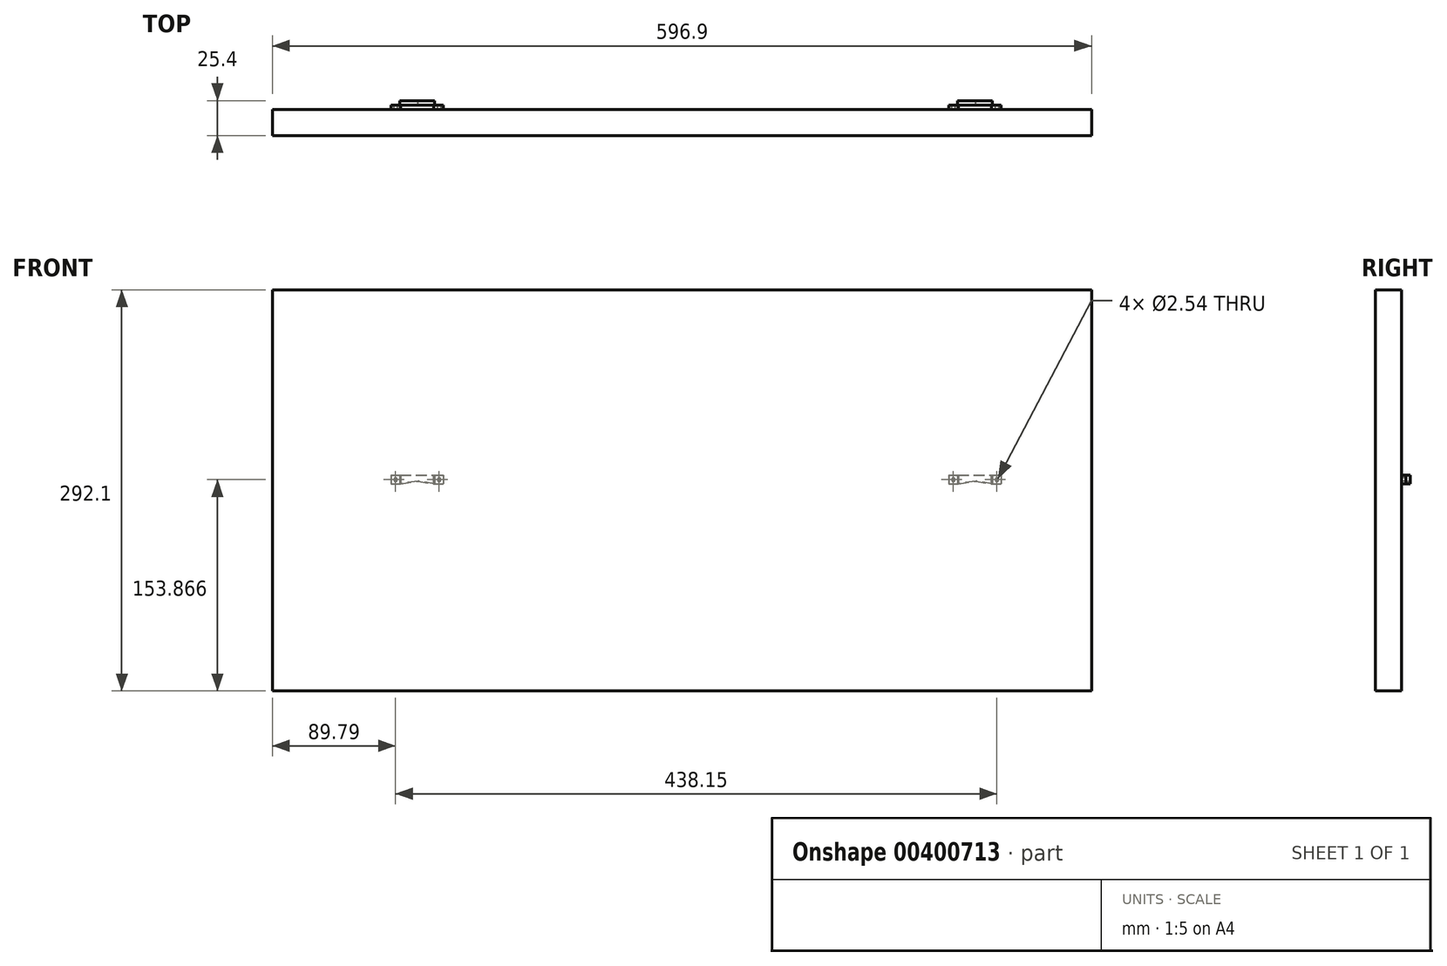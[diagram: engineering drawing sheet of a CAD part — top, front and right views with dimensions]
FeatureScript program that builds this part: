
annotation { "Feature Type Name" : "Feature", "Feature Type Description" : "" }
export const myFeature = defineFeature(function(context is Context, id is Id, definition is map)
    precondition{}
    {
        {
            var Q0;
            Q0=qCreatedBy(makeId("Front.planeOp"),FACE);
            var sketch = newSketch(context, id + "F0", { "sketchPlane" : qUnion([Q0])});
            skLineSegment(sketch, "E0.bottom", {"start": v(-19.44, 31.21) * mm, "end": v(18.66, 31.21) * mm});
            skLineSegment(sketch, "E0.top", {"start": v(-19.44, 24.86) * mm, "end": v(18.66, 24.86) * mm});
            skLineSegment(sketch, "E0.left", {"start": v(-19.44, 31.21) * mm, "end": v(-19.44, 24.86) * mm});
            skLineSegment(sketch, "E0.right", {"start": v(18.66, 31.21) * mm, "end": v(18.66, 24.86) * mm});
            skSolve(sketch);
        }
        {
            var Q0;
            Q0=makeQuery(id+"F0.imprint","IMPRINT",FACE,{"disambiguationData":[TD([[makeQuery(id+"F0.imprint","IMPRINT",EDGE,{"derivedFrom":sQuery(id+"F0.wireOp",EDGE,"E0.bottom")}),-1.0]])]});
            extrude(context, id + "F1", {"entities" : qUnion([Q0]), "depth" : 6.35 * mm});
        }
        {
            var Q0;
            Q0=makeQuery(id+"F1.opExtrude","CAP_FACE",FACE,{"disambiguationData":[OSD([sQuery(id+"F0.wireOp",EDGE,"E0.bottom"),sQuery(id+"F0.wireOp",EDGE,"E0.top"),sQuery(id+"F0.wireOp",EDGE,"E0.left"),sQuery(id+"F0.wireOp",EDGE,"E0.right")])],"isStart":false});
            var sketch = newSketch(context, id + "F2", { "sketchPlane" : qUnion([Q0])});
            skLineSegment(sketch, "E1", {"start": v(-19.44, 31.21) * mm, "end": v(-19.44, 24.86) * mm});
            skLineSegment(sketch, "E2", {"start": v(-19.44, 24.86) * mm, "end": v(-13.1, 24.86) * mm});
            skLineSegment(sketch, "E3", {"start": v(-13.1, 24.86) * mm, "end": v(-13.1, 31.21) * mm});
            skLineSegment(sketch, "E4", {"start": v(-13.1, 31.21) * mm, "end": v(-19.44, 31.21) * mm});
            skLineSegment(sketch, "E5", {"start": v(18.66, 31.21) * mm, "end": v(18.66, 24.86) * mm});
            skLineSegment(sketch, "E6", {"start": v(18.66, 24.86) * mm, "end": v(12.3, 24.86) * mm});
            skLineSegment(sketch, "E7", {"start": v(12.3, 24.86) * mm, "end": v(12.3, 31.21) * mm});
            skLineSegment(sketch, "E8", {"start": v(12.3, 31.21) * mm, "end": v(18.66, 31.21) * mm});
            skLineSegment(sketch, "E9", {"start": v(-12.5, 31.21) * mm, "end": v(-12.5, 24.86) * mm});
            skLineSegment(sketch, "E10", {"start": v(-12.5, 24.86) * mm, "end": v(11.64, 24.86) * mm});
            skLineSegment(sketch, "E11", {"start": v(11.64, 24.86) * mm, "end": v(11.64, 31.21) * mm});
            skSolve(sketch);
        }
        {
            var Q0;
            {var subQ0=sQuery(id+"F2.wireOp",EDGE,"E9");Q0=makeQuery(id+"F2.imprint","IMPRINT",FACE,{"disambiguationData":[TD([[makeQuery(id+"F2.imprint","IMPRINT",EDGE,{"derivedFrom":subQ0}),1.0]])]});}
            extrude(context, id + "F3", {"entities" : qUnion([Q0]), "operationType" : NewBodyOperationType.REMOVE, "oppositeDirection" : true, "depth" : 3.17 * mm});
        }
        {
            var Q0;
            Q0=makeQuery(id+"F1.opExtrude","CAP_FACE",FACE,{"disambiguationData":[OSD([sQuery(id+"F0.wireOp",EDGE,"E0.bottom"),sQuery(id+"F0.wireOp",EDGE,"E0.top"),sQuery(id+"F0.wireOp",EDGE,"E0.left"),sQuery(id+"F0.wireOp",EDGE,"E0.right")])],"isStart":true});
            var sketch = newSketch(context, id + "F4", { "sketchPlane" : qUnion([Q0])});
            skLineSegment(sketch, "E12", {"start": v(-18.66, 31.21) * mm, "end": v(-12.3, 31.21) * mm});
            skLineSegment(sketch, "E13", {"start": v(-12.3, 31.21) * mm, "end": v(-12.3, 24.86) * mm});
            skLineSegment(sketch, "E14", {"start": v(-12.3, 24.86) * mm, "end": v(-18.66, 24.86) * mm});
            skLineSegment(sketch, "E15", {"start": v(-18.66, 24.86) * mm, "end": v(-18.66, 31.21) * mm});
            skLineSegment(sketch, "E16", {"start": v(19.44, 31.21) * mm, "end": v(13.1, 31.21) * mm});
            skLineSegment(sketch, "E17", {"start": v(13.1, 31.21) * mm, "end": v(13.1, 24.86) * mm});
            skLineSegment(sketch, "E18", {"start": v(13.1, 24.86) * mm, "end": v(19.44, 24.86) * mm});
            skLineSegment(sketch, "E19", {"start": v(19.44, 24.86) * mm, "end": v(19.44, 30.76) * mm});
            skSolve(sketch);
        }
        {
            var Q0;
            Q0=makeQuery(id+"F4.imprint","IMPRINT",FACE,{"disambiguationData":[TD([[makeQuery(id+"F4.imprint","IMPRINT",EDGE,{"derivedFrom":sQuery(id+"F4.wireOp",EDGE,"E12")}),1.0]])]});
            var Q1;
            {var subQ1=sQuery(id+"F4.wireOp",EDGE,"E16");Q1=makeQuery(id+"F4.imprint","IMPRINT",FACE,{"disambiguationData":[TD([[makeQuery(id+"F4.imprint","IMPRINT",EDGE,{"derivedFrom":subQ1}),1.0]])]});}
            extrude(context, id + "F5", {"entities" : qUnion([Q0, Q1]), "operationType" : NewBodyOperationType.REMOVE, "oppositeDirection" : true, "depth" : 3.17 * mm});
        }
        {
            var Q0;
            Q0=makeQuery(id+"F1.opExtrude","CAP_FACE",FACE,{"disambiguationData":[OSD([sQuery(id+"F0.wireOp",EDGE,"E0.bottom"),sQuery(id+"F0.wireOp",EDGE,"E0.top"),sQuery(id+"F0.wireOp",EDGE,"E0.left"),sQuery(id+"F0.wireOp",EDGE,"E0.right")])],"isStart":true});
            var sketch = newSketch(context, id + "F6", { "sketchPlane" : qUnion([Q0])});
            skLineSegment(sketch, "E20", {"start": v(-12.3, 24.86) * mm, "end": v(0, 26.97) * mm});
            skLineSegment(sketch, "E21", {"start": v(0, 26.97) * mm, "end": v(13.1, 24.86) * mm});
            skSolve(sketch);
        }
        {
            var Q0;
            {var subQ0=sQuery(id+"F0.wireOp",EDGE,"E0.bottom");var subQ1=sQuery(id+"F0.wireOp",EDGE,"E0.top");var subQ2=sQuery(id+"F0.wireOp",EDGE,"E0.left");Q0=makeQuery(id+"F3.boolean.opBoolean","SPLIT",FACE,{"disambiguationData":[TD([makeQuery(id+"F1.opExtrude","SWEPT_FACE",FACE,{"disambiguationData":[OSD([subQ2])]})])],"derivedFrom":makeQuery(id+"F1.opExtrude","CAP_FACE",FACE,{"disambiguationData":[OSD([subQ0,subQ1,subQ2,sQuery(id+"F0.wireOp",EDGE,"E0.right")])],"isStart":false})});}
            var sketch = newSketch(context, id + "F7", { "sketchPlane" : qUnion([Q0])});
            skCircle(sketch, "E22", {"center": v(-16.27, 28.04) * mm, "radius": 1.27 * mm});
            skCircle(sketch, "E23", {"center": v(15.48, 28.04) * mm, "radius": 1.27 * mm});
            skPoint(sketch, "E23.centerSnap0", {"position": v(-19.44, 28.04) * mm});
            skSolve(sketch);
        }
        {
            var Q0;
            Q0=makeQuery(id+"F7.imprint","IMPRINT",FACE,{"disambiguationData":[TD([[makeQuery(id+"F7.imprint","IMPRINT",EDGE,{"derivedFrom":sQuery(id+"F7.wireOp",EDGE,"E22")}),1.0]])]});
            var Q1;
            Q1=makeQuery(id+"F7.imprint","IMPRINT",FACE,{"disambiguationData":[TD([[makeQuery(id+"F7.imprint","IMPRINT",EDGE,{"derivedFrom":sQuery(id+"F7.wireOp",EDGE,"E23")}),1.0]])]});
            extrude(context, id + "F8", {"entities" : qUnion([Q0, Q1]), "operationType" : NewBodyOperationType.REMOVE, "oppositeDirection" : true, "depth" : 6.35 * mm});
        }
        {
            var Q0;
            Q0=makeQuery(id+"F6.imprint","IMPRINT",FACE,{"disambiguationData":[TD([[makeQuery(id+"F6.imprint","IMPRINT",EDGE,{"derivedFrom":sQuery(id+"F6.wireOp",EDGE,"E20")}),-1.0]])]});
            extrude(context, id + "F9", {"entities" : qUnion([Q0]), "operationType" : NewBodyOperationType.REMOVE, "oppositeDirection" : true, "depth" : 25.4 * mm});
        }
        {
            var Q0;
            Q0=qCreatedBy(makeId("Front.planeOp"),FACE);
            cPlane(context, id + "F10", {"entities" : qUnion([Q0]), "cplaneType" : CPlaneType.OFFSET, "offset" : 6.35 * mm, "width" : 152.4 * mm, "height" : 152.4 * mm});
        }
        {
            var Q0;
            Q0=qCreatedBy(id+"F10.planeOp",FACE);
            var sketch = newSketch(context, id + "F11", { "sketchPlane" : qUnion([Q0])});
            skLineSegment(sketch, "E24.bottom", {"start": v(-258.46, 166.27) * mm, "end": v(338.44, 166.27) * mm});
            skLineSegment(sketch, "E24.top", {"start": v(-258.46, -125.83) * mm, "end": v(338.44, -125.83) * mm});
            skLineSegment(sketch, "E24.left", {"start": v(-258.46, 166.27) * mm, "end": v(-258.46, -125.83) * mm});
            skLineSegment(sketch, "E24.right", {"start": v(338.44, 166.27) * mm, "end": v(338.44, -125.83) * mm});
            skSolve(sketch);
        }
        {
            var Q0;
            Q0=makeQuery(id+"F11.imprint","IMPRINT",FACE,{"disambiguationData":[TD([[makeQuery(id+"F11.imprint","IMPRINT",EDGE,{"derivedFrom":sQuery(id+"F11.wireOp",EDGE,"E24.bottom")}),-1.0]])]});
            extrude(context, id + "F12", {"entities" : qUnion([Q0]), "depth" : 19.05 * mm});
        }
        {
            var Q0;
            Q0=makeQuery(id+"F1.opExtrude","SWEPT_BODY",BODY,{"disambiguationData":[OSD([sQuery(id+"F0.wireOp",EDGE,"E0.bottom"),sQuery(id+"F0.wireOp",EDGE,"E0.top"),sQuery(id+"F0.wireOp",EDGE,"E0.left"),sQuery(id+"F0.wireOp",EDGE,"E0.right")])]});
            var Q1;
            Q1=makeQuery(id+"F12.opExtrude","CAP_EDGE",EDGE,{"disambiguationData":[OSD([sQuery(id+"F11.wireOp",EDGE,"E24.bottom")])],"isStart":true});
            transform(context, id + "F13", {"entities" : qUnion([Q0]), "transformType" : TransformType.TRANSLATION_DISTANCE, "transformDirection" : qUnion([Q1]), "distance" : 254 * mm, "makeCopy" : true});
        }
        {
            var Q0;
            Q0=makeQuery(id+"F1.opExtrude","SWEPT_BODY",BODY,{"disambiguationData":[OSD([sQuery(id+"F0.wireOp",EDGE,"E0.bottom"),sQuery(id+"F0.wireOp",EDGE,"E0.top"),sQuery(id+"F0.wireOp",EDGE,"E0.left"),sQuery(id+"F0.wireOp",EDGE,"E0.right")])]});
            var Q1;
            Q1=makeQuery(id+"F12.opExtrude","CAP_EDGE",EDGE,{"disambiguationData":[OSD([sQuery(id+"F11.wireOp",EDGE,"E24.bottom")])],"isStart":true});
            transform(context, id + "F14", {"entities" : qUnion([Q0]), "transformType" : TransformType.TRANSLATION_DISTANCE, "transformDirection" : qUnion([Q1]), "distance" : 127 * mm, "oppositeDirection" : true, "makeCopy" : false});
        }
        {
            var Q0;
            Q0=makeQuery(id+"F1.opExtrude","SWEPT_BODY",BODY,{"disambiguationData":[OSD([sQuery(id+"F0.wireOp",EDGE,"E0.bottom"),sQuery(id+"F0.wireOp",EDGE,"E0.top"),sQuery(id+"F0.wireOp",EDGE,"E0.left"),sQuery(id+"F0.wireOp",EDGE,"E0.right")])]});
            var Q1;
            Q1=makeQuery(id+"F12.opExtrude","CAP_EDGE",EDGE,{"disambiguationData":[OSD([sQuery(id+"F11.wireOp",EDGE,"E24.bottom")])],"isStart":true});
            transform(context, id + "F15", {"entities" : qUnion([Q0]), "transformType" : TransformType.TRANSLATION_DISTANCE, "transformDirection" : qUnion([Q1]), "distance" : 25.4 * mm, "oppositeDirection" : true, "makeCopy" : false});
        }
    });
